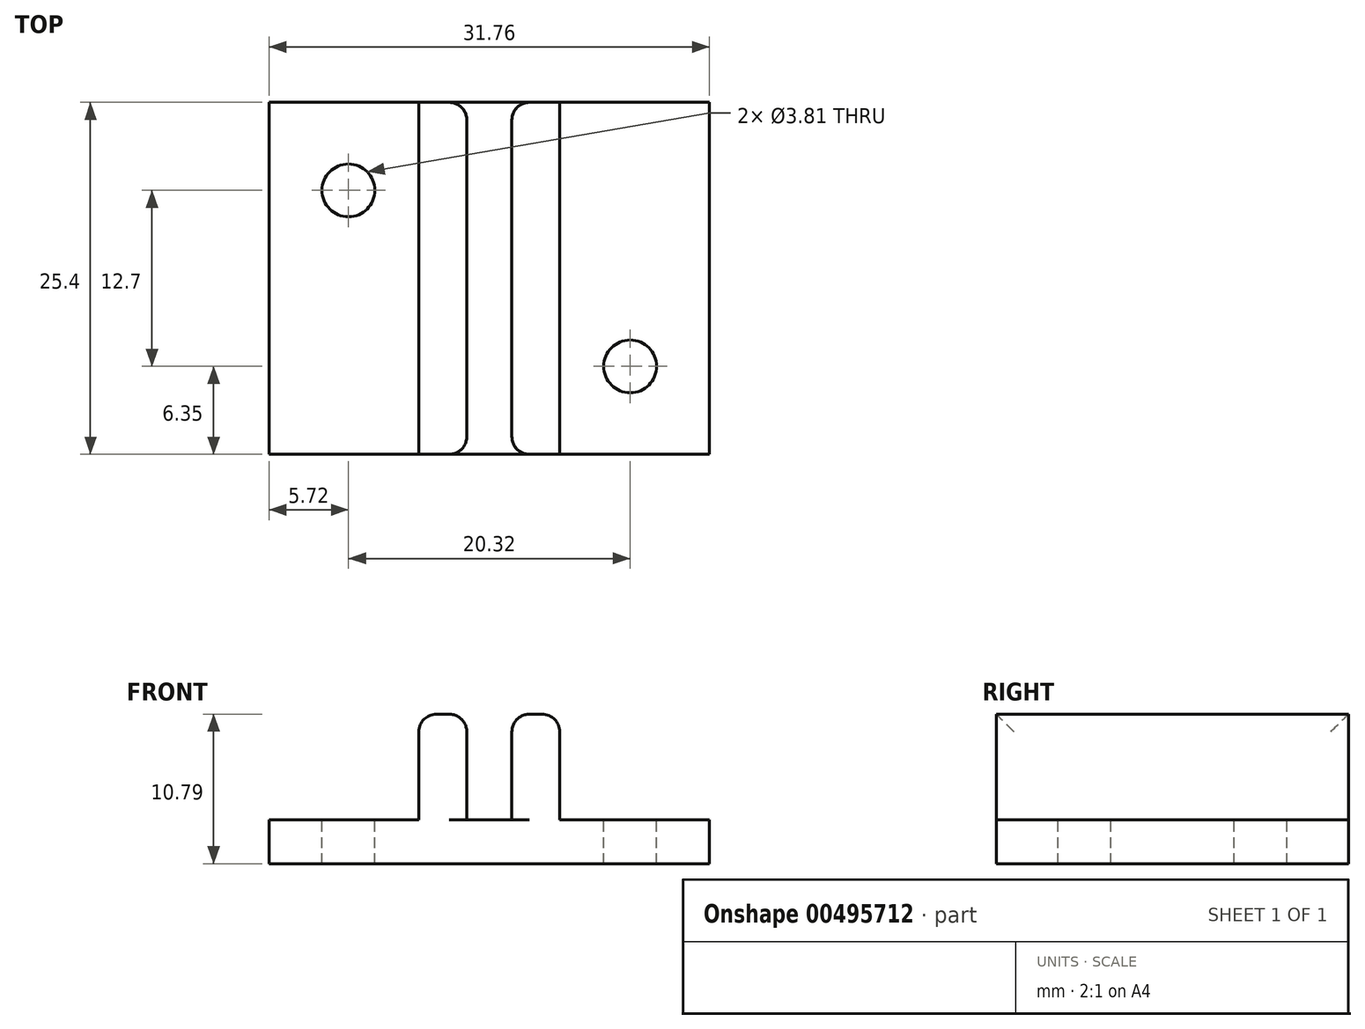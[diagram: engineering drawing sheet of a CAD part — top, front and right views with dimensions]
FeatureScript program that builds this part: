
annotation { "Feature Type Name" : "Feature", "Feature Type Description" : "" }
export const myFeature = defineFeature(function(context is Context, id is Id, definition is map)
    precondition{}
    {
        {
            var Q0;
            Q0=qCreatedBy(makeId("Top.planeOp"),FACE);
            var sketch = newSketch(context, id + "F0", { "sketchPlane" : qUnion([Q0])});
            skLineSegment(sketch, "E0.bottom", {"start": v(15.88, 12.7) * mm, "end": v(-15.88, 12.7) * mm});
            skLineSegment(sketch, "E0.top", {"start": v(15.88, -12.7) * mm, "end": v(-15.88, -12.7) * mm});
            skLineSegment(sketch, "E0.left", {"start": v(15.88, 12.7) * mm, "end": v(15.88, -12.7) * mm});
            skLineSegment(sketch, "E0.right", {"start": v(-15.88, 12.7) * mm, "end": v(-15.88, -12.7) * mm});
            skPoint(sketch, "E0.middle", {"position": v(0, 0) * mm});
            skSolve(sketch);
        }
        {
            var Q0;
            Q0=makeQuery(id+"F0.imprint","IMPRINT",FACE,{"disambiguationData":[TD([[makeQuery(id+"F0.imprint","IMPRINT",EDGE,{"derivedFrom":sQuery(id+"F0.wireOp",EDGE,"E0.bottom")}),1.0]])]});
            extrude(context, id + "F1", {"entities" : qUnion([Q0]), "depth" : 3.17 * mm});
        }
        {
            var Q0;
            Q0=makeQuery(id+"F1.opExtrude","CAP_FACE",FACE,{"disambiguationData":[OSD([sQuery(id+"F0.wireOp",EDGE,"E0.bottom"),sQuery(id+"F0.wireOp",EDGE,"E0.top"),sQuery(id+"F0.wireOp",EDGE,"E0.left"),sQuery(id+"F0.wireOp",EDGE,"E0.right")])],"isStart":false});
            var sketch = newSketch(context, id + "F2", { "sketchPlane" : qUnion([Q0])});
            skLineSegment(sketch, "E1.bottom", {"start": v(5.08, 12.7) * mm, "end": v(-5.08, 12.7) * mm});
            skLineSegment(sketch, "E1.top", {"start": v(5.08, -12.7) * mm, "end": v(-5.08, -12.7) * mm});
            skLineSegment(sketch, "E1.left", {"start": v(5.08, 12.7) * mm, "end": v(5.08, -12.7) * mm});
            skLineSegment(sketch, "E1.right", {"start": v(-5.08, 12.7) * mm, "end": v(-5.08, -12.7) * mm});
            skPoint(sketch, "E1.middle", {"position": v(0, 0) * mm});
            skLineSegment(sketch, "E2.bottom", {"start": v(1.63, 12.7) * mm, "end": v(-1.63, 12.7) * mm});
            skLineSegment(sketch, "E2.top", {"start": v(1.63, -12.7) * mm, "end": v(-1.63, -12.7) * mm});
            skLineSegment(sketch, "E2.left", {"start": v(1.63, 12.7) * mm, "end": v(1.63, -12.7) * mm});
            skLineSegment(sketch, "E2.right", {"start": v(-1.63, 12.7) * mm, "end": v(-1.63, -12.7) * mm});
            skSolve(sketch);
        }
        {
            var Q0;
            {var subQ0=sQuery(id+"F2.wireOp",EDGE,"E1.right");Q0=makeQuery(id+"F2.imprint","IMPRINT",FACE,{"disambiguationData":[TD([[makeQuery(id+"F2.imprint","IMPRINT",EDGE,{"derivedFrom":subQ0}),1.0]])]});}
            var Q1;
            {var subQ0=sQuery(id+"F2.wireOp",EDGE,"E1.left");Q1=makeQuery(id+"F2.imprint","IMPRINT",FACE,{"disambiguationData":[TD([[makeQuery(id+"F2.imprint","IMPRINT",EDGE,{"derivedFrom":subQ0}),-1.0]])]});}
            extrude(context, id + "F3", {"entities" : qUnion([Q0, Q1]), "operationType" : NewBodyOperationType.ADD, "depth" : 7.62 * mm});
        }
        {
            var Q0;
            Q0=makeQuery(id+"F3.opExtrude","CAP_EDGE",EDGE,{"disambiguationData":[OSD([sQuery(id+"F2.wireOp",EDGE,"E2.right")])],"isStart":false});
            var Q1;
            Q1=makeQuery(id+"F3.opExtrude","CAP_EDGE",EDGE,{"disambiguationData":[OSD([sQuery(id+"F2.wireOp",EDGE,"E1.right")])],"isStart":false});
            var Q2;
            Q2=makeQuery(id+"F3.opExtrude","CAP_EDGE",EDGE,{"disambiguationData":[OSD([sQuery(id+"F2.wireOp",EDGE,"E2.left")])],"isStart":false});
            var Q3;
            Q3=makeQuery(id+"F3.opExtrude","CAP_EDGE",EDGE,{"disambiguationData":[OSD([sQuery(id+"F2.wireOp",EDGE,"E1.left")])],"isStart":false});
            var Q4;
            Q4=makeQuery(id+"F3.opExtrude","SWEPT_EDGE",EDGE,{"disambiguationData":[OSD([sQuery(id+"F2.wireOp",EDGE,"E1.bottom"),sQuery(id+"F2.wireOp",EDGE,"E2.bottom"),sQuery(id+"F2.wireOp",EDGE,"E2.left")])]});
            var Q5;
            Q5=makeQuery(id+"F3.opExtrude","SWEPT_EDGE",EDGE,{"disambiguationData":[OSD([sQuery(id+"F2.wireOp",EDGE,"E1.bottom"),sQuery(id+"F2.wireOp",EDGE,"E2.bottom"),sQuery(id+"F2.wireOp",EDGE,"E2.right")])]});
            var Q6;
            Q6=makeQuery(id+"F3.opExtrude","SWEPT_EDGE",EDGE,{"disambiguationData":[OSD([sQuery(id+"F2.wireOp",EDGE,"E1.top"),sQuery(id+"F2.wireOp",EDGE,"E2.top"),sQuery(id+"F2.wireOp",EDGE,"E2.left")])]});
            var Q7;
            Q7=makeQuery(id+"F3.opExtrude","SWEPT_EDGE",EDGE,{"disambiguationData":[OSD([sQuery(id+"F2.wireOp",EDGE,"E1.top"),sQuery(id+"F2.wireOp",EDGE,"E2.top"),sQuery(id+"F2.wireOp",EDGE,"E2.right")])]});
            fillet(context, id + "F4", {"entities" : qUnion([Q0, Q1, Q2, Q3, Q4, Q5, Q6, Q7]), "radius" : 1.27 * mm, "tangentPropagation" : true, "allowEdgeOverflow" : false});
        }
        {
            var Q0;
            {var subQ2=sQuery(id+"F0.wireOp",EDGE,"E0.bottom");var subQ6=sQuery(id+"F0.wireOp",EDGE,"E0.top");var subQ7=sQuery(id+"F0.wireOp",EDGE,"E0.right");Q0=makeQuery(id+"F3.boolean.opBoolean","SPLIT",FACE,{"disambiguationData":[TD([makeQuery(id+"F1.opExtrude","SWEPT_FACE",FACE,{"disambiguationData":[OSD([subQ7])]})])],"derivedFrom":makeQuery(id+"F1.opExtrude","CAP_FACE",FACE,{"disambiguationData":[OSD([subQ2,subQ6,sQuery(id+"F0.wireOp",EDGE,"E0.left"),subQ7])],"isStart":false})});}
            var sketch = newSketch(context, id + "F5", { "sketchPlane" : qUnion([Q0])});
            skCircle(sketch, "E3", {"center": v(-10.16, 6.35) * mm, "radius": 1.9 * mm});
            skCircle(sketch, "E4", {"center": v(10.16, -6.35) * mm, "radius": 1.9 * mm});
            skSolve(sketch);
        }
        {
            var Q0;
            Q0=makeQuery(id+"F5.imprint","IMPRINT",FACE,{"disambiguationData":[TD([[makeQuery(id+"F5.imprint","IMPRINT",EDGE,{"derivedFrom":sQuery(id+"F5.wireOp",EDGE,"E3")}),1.0]])]});
            var Q1;
            Q1=makeQuery(id+"F5.imprint","IMPRINT",FACE,{"disambiguationData":[TD([[makeQuery(id+"F5.imprint","IMPRINT",EDGE,{"derivedFrom":sQuery(id+"F5.wireOp",EDGE,"E4")}),1.0]])]});
            var Q2;
            Q2=makeQuery(id+"F1.opExtrude","CAP_FACE",FACE,{"disambiguationData":[OSD([sQuery(id+"F0.wireOp",EDGE,"E0.bottom"),sQuery(id+"F0.wireOp",EDGE,"E0.top"),sQuery(id+"F0.wireOp",EDGE,"E0.left"),sQuery(id+"F0.wireOp",EDGE,"E0.right")])],"isStart":true});
            extrude(context, id + "F6", {"entities" : qUnion([Q0, Q1]), "operationType" : NewBodyOperationType.REMOVE, "endBound" : BoundingType.UP_TO_SURFACE, "oppositeDirection" : true, "endBoundEntityFace" : qUnion([Q2]), "depth" : 25.4 * mm});
        }
    });
